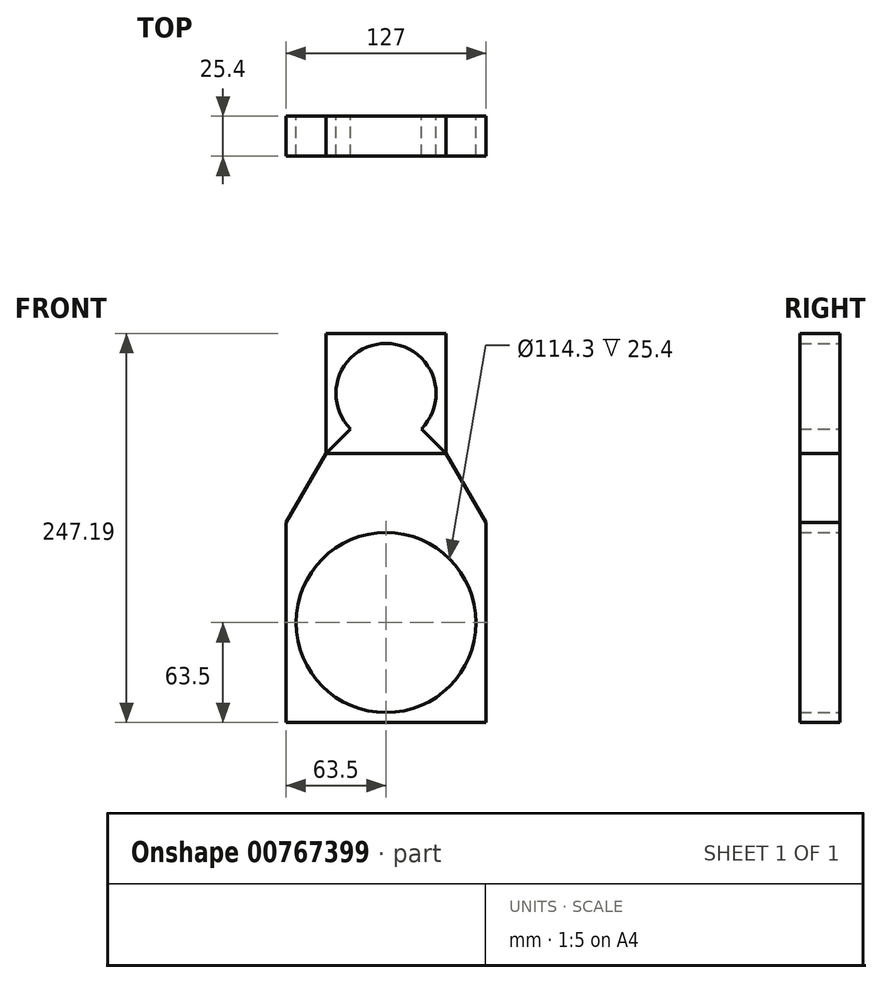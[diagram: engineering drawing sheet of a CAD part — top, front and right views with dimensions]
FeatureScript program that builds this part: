
annotation { "Feature Type Name" : "Feature", "Feature Type Description" : "" }
export const myFeature = defineFeature(function(context is Context, id is Id, definition is map)
    precondition{}
    {
        {
            var Q0;
            Q0=qCreatedBy(makeId("Front.planeOp"),FACE);
            var sketch = newSketch(context, id + "F0", { "sketchPlane" : qUnion([Q0])});
            skLineSegment(sketch, "E0.bottom", {"start": v(0, 0) * mm, "end": v(127, 0) * mm});
            skLineSegment(sketch, "E0.top", {"start": v(0, -127) * mm, "end": v(127, -127) * mm});
            skLineSegment(sketch, "E0.left", {"start": v(0, 0) * mm, "end": v(0, -127) * mm});
            skLineSegment(sketch, "E0.right", {"start": v(127, 0) * mm, "end": v(127, -127) * mm});
            skLineSegment(sketch, "E1", {"start": v(0, 0) * mm, "end": v(25.4, 44) * mm});
            skLineSegment(sketch, "E2", {"start": v(25.4, 44) * mm, "end": v(101.6, 44) * mm});
            skLineSegment(sketch, "E3", {"start": v(101.6, 44) * mm, "end": v(127, 0) * mm});
            skLineSegment(sketch, "E4.top", {"start": v(25.4, 120.2) * mm, "end": v(101.6, 120.2) * mm});
            skLineSegment(sketch, "E4.left", {"start": v(25.4, 44) * mm, "end": v(25.4, 120.2) * mm});
            skLineSegment(sketch, "E4.right", {"start": v(101.6, 44) * mm, "end": v(101.6, 120.2) * mm});
            skLineSegment(sketch, "E5", {"start": v(0, 0) * mm, "end": v(127, -127) * mm});
            skLineSegment(sketch, "E6", {"start": v(127, 0) * mm, "end": v(0, -127) * mm});
            skLineSegment(sketch, "E7", {"start": v(25.4, 120.2) * mm, "end": v(101.6, 44) * mm});
            skLineSegment(sketch, "E8", {"start": v(101.6, 120.2) * mm, "end": v(25.4, 44) * mm});
            skCircle(sketch, "E9", {"center": v(63.5, -63.5) * mm, "radius": 57.15 * mm});
            skCircle(sketch, "E10", {"center": v(63.5, 82.1) * mm, "radius": 31.75 * mm});
            skSolve(sketch);
        }
        {
            var Q0;
            Q0=makeQuery(id+"F0.imprint","IMPRINT",FACE,{"disambiguationData":[TD([[makeQuery(id+"F0.imprint","IMPRINT",EDGE,{"derivedFrom":sQuery(id+"F0.wireOp",EDGE,"E0.bottom")}),1.0]])]});
            var Q1;
            {var subQ0=sQuery(id+"F0.wireOp",EDGE,"E0.top");Q1=makeQuery(id+"F0.imprint","IMPRINT",FACE,{"disambiguationData":[TD([[makeQuery(id+"F0.imprint","IMPRINT",EDGE,{"derivedFrom":subQ0}),1.0]])]});}
            var Q2;
            {var subQ0=sQuery(id+"F0.wireOp",EDGE,"E0.left");Q2=makeQuery(id+"F0.imprint","IMPRINT",FACE,{"disambiguationData":[TD([[makeQuery(id+"F0.imprint","IMPRINT",EDGE,{"derivedFrom":subQ0}),1.0]])]});}
            var Q3;
            {var subQ0=sQuery(id+"F0.wireOp",EDGE,"E0.right");Q3=makeQuery(id+"F0.imprint","IMPRINT",FACE,{"disambiguationData":[TD([[makeQuery(id+"F0.imprint","IMPRINT",EDGE,{"derivedFrom":subQ0}),-1.0]])]});}
            var Q4;
            {var subQ0=sQuery(id+"F0.wireOp",EDGE,"E4.left");Q4=makeQuery(id+"F0.imprint","IMPRINT",FACE,{"disambiguationData":[TD([[makeQuery(id+"F0.imprint","IMPRINT",EDGE,{"derivedFrom":subQ0}),-1.0]])]});}
            var Q5;
            {var subQ0=sQuery(id+"F0.wireOp",EDGE,"E4.right");Q5=makeQuery(id+"F0.imprint","IMPRINT",FACE,{"disambiguationData":[TD([[makeQuery(id+"F0.imprint","IMPRINT",EDGE,{"derivedFrom":subQ0}),1.0]])]});}
            var Q6;
            {var subQ0=sQuery(id+"F0.wireOp",EDGE,"E0.bottom");Q6=makeQuery(id+"F0.imprint","IMPRINT",FACE,{"disambiguationData":[TD([[makeQuery(id+"F0.imprint","IMPRINT",EDGE,{"derivedFrom":subQ0}),-1.0]])]});}
            var Q7;
            {var subQ0=sQuery(id+"F0.wireOp",EDGE,"E2");Q7=makeQuery(id+"F0.imprint","IMPRINT",FACE,{"disambiguationData":[TD([[makeQuery(id+"F0.imprint","IMPRINT",EDGE,{"derivedFrom":subQ0}),1.0]])]});}
            var Q8;
            {var subQ0=sQuery(id+"F0.wireOp",EDGE,"E4.top");Q8=makeQuery(id+"F0.imprint","IMPRINT",FACE,{"disambiguationData":[TD([[makeQuery(id+"F0.imprint","IMPRINT",EDGE,{"derivedFrom":subQ0}),-1.0]])]});}
            extrude(context, id + "F1", {"entities" : qUnion([Q0, Q1, Q2, Q3, Q4, Q5, Q6, Q7, Q8]), "depth" : 25.4 * mm, "offsetDistance" : 25.4 * mm});
        }
    });
